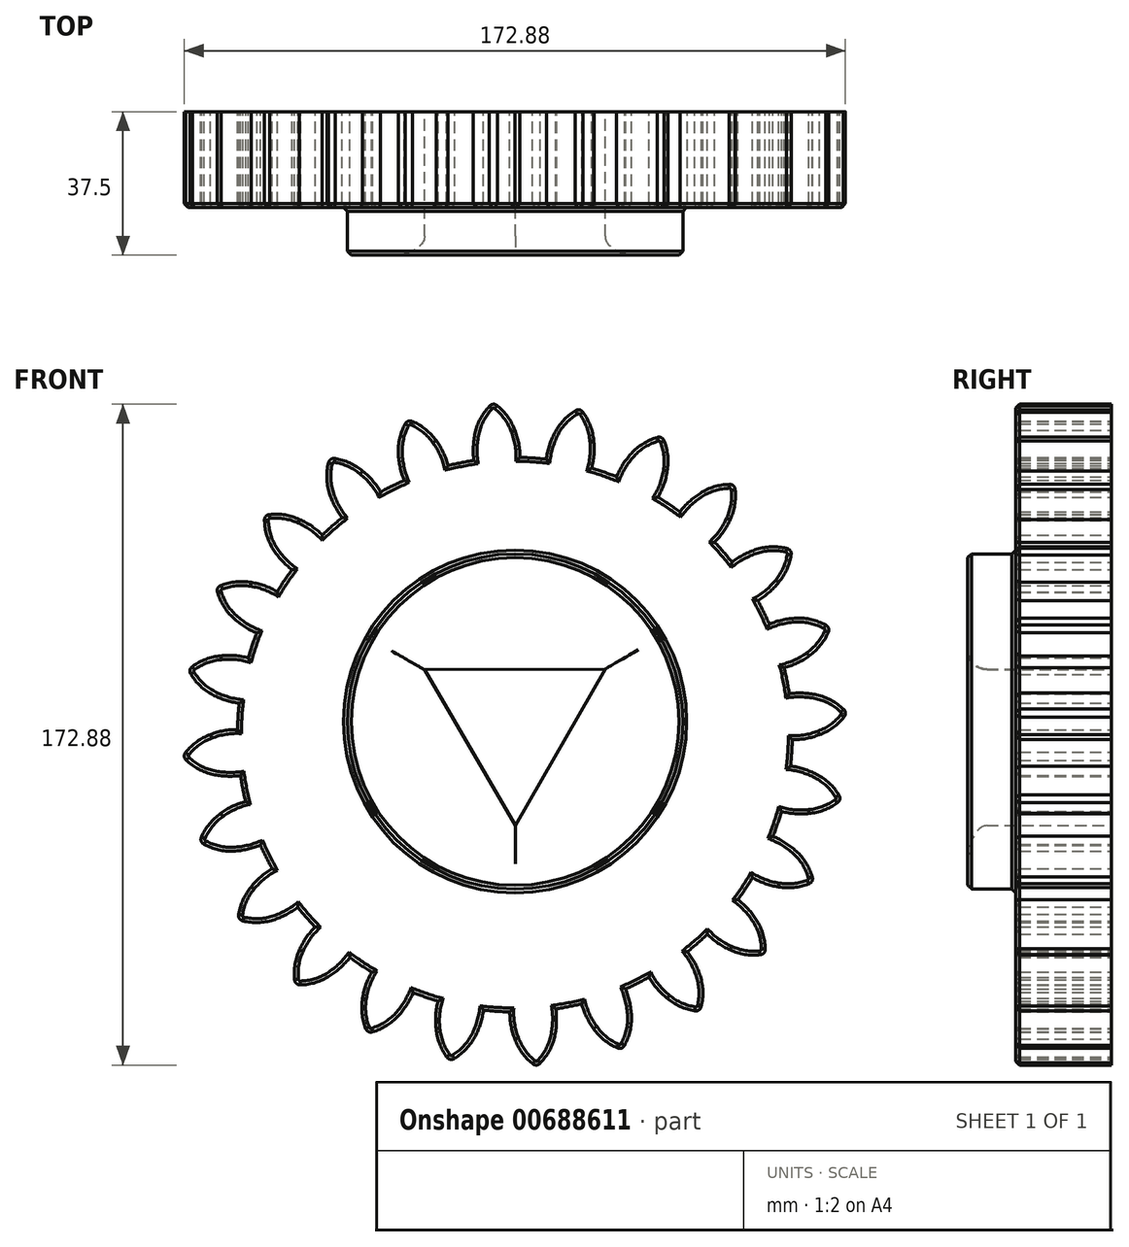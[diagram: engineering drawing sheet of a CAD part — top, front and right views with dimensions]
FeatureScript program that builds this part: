
annotation { "Feature Type Name" : "Feature", "Feature Type Description" : "" }
export const myFeature = defineFeature(function(context is Context, id is Id, definition is map)
    precondition{}
    {
        {
            var Q0;
            Q0=qCreatedBy(makeId("Front.planeOp"),FACE);
            var sketch = newSketch(context, id + "F0", { "sketchPlane" : qUnion([Q0])});
            skCircle(sketch, "E0", {"center": v(-0.05, -3.44) * mm, "radius": 86.16 * mm, "construction": true});
            skCircle(sketch, "E1", {"center": v(-0.05, -3.44) * mm, "radius": 79.67 * mm, "construction": true});
            skCircle(sketch, "E2", {"center": v(-0.05, -3.44) * mm, "radius": 72.52 * mm});
            skLineSegment(sketch, "E3", {"start": v(-0.05, -3.44) * mm, "end": v(-0.05, 109) * mm, "construction": true});
            skLineSegment(sketch, "E4", {"start": v(-0.05, -3.44) * mm, "end": v(-7.36, 108.12) * mm, "construction": true});
            skCircle(sketch, "E5", {"center": v(-0.05, -3.44) * mm, "radius": 74.83 * mm, "construction": true});
            skLineSegment(sketch, "E6", {"start": v(-0.05, 76.19) * mm, "end": v(-82.1, 46.32) * mm, "construction": true});
            skLineSegment(sketch, "E7", {"start": v(-0.05, 76.19) * mm, "end": v(-80.24, 76.19) * mm, "construction": true});
            skCircle(sketch, "E8", {"center": v(-0.05, 76.19) * mm, "radius": 14.6 * mm, "construction": true});
            skCircle(sketch, "E9", {"center": v(-13.78, 71.2) * mm, "radius": 14.6 * mm, "construction": true});
            skArc(sketch, "E10", {"start": v(-0.05, 76.19) * mm, "mid": v(-1.9, 79.7) * mm, "end": v(-4.65, 82.6) * mm});
            skArc(sketch, "E11.MirrorCS", {"start": v(-10.45, 75.5) * mm, "mid": v(-9.06, 79.24) * mm, "end": v(-6.73, 82.46) * mm});
            skArc(sketch, "E12", {"start": v(-4.65, 82.6) * mm, "mid": v(-5.72, 83) * mm, "end": v(-6.73, 82.46) * mm});
            skArc(sketch, "E13", {"start": v(-10.45, 75.5) * mm, "mid": v(-10.91, 71.91) * mm, "end": v(-10.77, 68.29) * mm});
            skArc(sketch, "E14", {"start": v(1.27, 69.07) * mm, "mid": v(0.96, 72.7) * mm, "end": v(-0.05, 76.19) * mm});
            skPoint(sketch, "E15.0.midPoint", {"position": v(-0.05, 17.48) * mm});
            skCircle(sketch, "E16", {"center": v(0, 0) * mm, "radius": 48.64 * mm});
            skCircle(sketch, "E17.cCircle", {"center": v(0, 0) * mm, "radius": 13.62 * mm, "construction": true});
            skLineSegment(sketch, "E17.0", {"start": v(-23.64, 13.53) * mm, "end": v(23.53, 13.7) * mm});
            skLineSegment(sketch, "E17.1", {"start": v(23.53, 13.7) * mm, "end": v(0.1, -27.23) * mm});
            skLineSegment(sketch, "E17.2", {"start": v(0.1, -27.23) * mm, "end": v(-23.64, 13.53) * mm});
            skPoint(sketch, "E17.0.midPoint", {"position": v(-0.05, 13.62) * mm});
            skSolve(sketch);
        }
        {
            var Q0;
            {var subQ0=sQuery(id+"F0.wireOp",EDGE,"E2");var subQ1=makeQuery(id+"F0.imprint","INTERSECT",VERTEX,{"derivedFrom":[subQ0,sQuery(id+"F0.wireOp",EDGE,"E13")]});Q0=makeQuery(id+"F0.imprint","IMPRINT",FACE,{"disambiguationData":[TD([[makeQuery(id+"F0.imprint","IMPRINT",EDGE,{"disambiguationData":[TD([[subQ1,1.0]])],"derivedFrom":subQ0}),1.0]])]});}
            var Q1;
            Q1=makeQuery(id+"F0.imprint","IMPRINT",FACE,{"disambiguationData":[TD([[makeQuery(id+"F0.imprint","IMPRINT",EDGE,{"derivedFrom":sQuery(id+"F0.wireOp",EDGE,"E10")}),1.0]])]});
            var Q2;
            Q2=makeQuery(id+"F0.imprint","IMPRINT",FACE,{"disambiguationData":[TD([[makeQuery(id+"F0.imprint","IMPRINT",EDGE,{"derivedFrom":sQuery(id+"F0.wireOp",EDGE,"E16")}),1.0]])]});
            extrude(context, id + "F1", {"entities" : qUnion([Q0, Q1, Q2]), "endBound" : BoundingType.SYMMETRIC, "depth" : 25 * mm, "offsetDistance" : 25 * mm});
        }
        {
            var Q0;
            Q0=makeQuery(id+"F1.opExtrude","SWEPT_BODY",BODY,{"disambiguationData":[OSD([sQuery(id+"F0.wireOp",EDGE,"E2"),sQuery(id+"F0.wireOp",EDGE,"E10"),sQuery(id+"F0.wireOp",EDGE,"E11.MirrorCS"),sQuery(id+"F0.wireOp",EDGE,"E12"),sQuery(id+"F0.wireOp",EDGE,"E13"),sQuery(id+"F0.wireOp",EDGE,"E14")])]});
            var Q1;
            Q1=makeQuery(id+"F1.opExtrude","SWEPT_FACE",FACE,{"disambiguationData":[OSD([sQuery(id+"F0.wireOp",EDGE,"E2")])]});
            circularPattern(context, id + "F2", {"entities" : qUnion([Q0]), "axis" : qUnion([Q1]), "angle" : 360 * degree, "instanceCount" : 24, "equalSpace" : true});
        }
        {
            var Q0;
            Q0=makeQuery(id+"F1.opExtrude","CAP_FACE",FACE,{"disambiguationData":[OSD([sQuery(id+"F0.wireOp",EDGE,"E2"),sQuery(id+"F0.wireOp",EDGE,"E10"),sQuery(id+"F0.wireOp",EDGE,"E11.MirrorCS"),sQuery(id+"F0.wireOp",EDGE,"E12"),sQuery(id+"F0.wireOp",EDGE,"E13"),sQuery(id+"F0.wireOp",EDGE,"E14"),sQuery(id+"F0.wireOp",EDGE,"E17.0"),sQuery(id+"F0.wireOp",EDGE,"E17.1"),sQuery(id+"F0.wireOp",EDGE,"E17.2")])],"isStart":false});
            var sketch = newSketch(context, id + "F3", { "sketchPlane" : qUnion([Q0])});
            skCircle(sketch, "E18", {"center": v(0, 0) * mm, "radius": 43.85 * mm});
            skSolve(sketch);
        }
        {
            var Q0;
            Q0=makeQuery(id+"F3.imprint","IMPRINT",FACE,{"disambiguationData":[TD([[makeQuery(id+"F3.imprint","IMPRINT",EDGE,{"derivedFrom":sQuery(id+"F3.wireOp",EDGE,"E18")}),1.0]])]});
            extrude(context, id + "F4", {"entities" : qUnion([Q0]), "operationType" : NewBodyOperationType.ADD, "endBound" : BoundingType.SYMMETRIC, "depth" : 25 * mm, "offsetDistance" : 25 * mm});
        }
        {
            var Q0;
            Q0=makeQuery(id+"F4.opExtrude","CAP_EDGE",EDGE,{"disambiguationData":[OSD([sQuery(id+"F0.wireOp",EDGE,"E17.0")])],"isStart":false});
            var Q1;
            Q1=makeQuery(id+"F4.opExtrude","CAP_EDGE",EDGE,{"disambiguationData":[OSD([sQuery(id+"F0.wireOp",EDGE,"E17.2")])],"isStart":false});
            var Q2;
            Q2=makeQuery(id+"F4.opExtrude","CAP_EDGE",EDGE,{"disambiguationData":[OSD([sQuery(id+"F0.wireOp",EDGE,"E17.1")])],"isStart":false});
            fillet(context, id + "F5", {"entities" : qUnion([Q0, Q1, Q2]), "radius" : 5 * mm, "tangentPropagation" : true, "allowEdgeOverflow" : false});
        }
        {
            var Q0;
            {var subQ0=makeQuery(id+"F1.opExtrude","CAP_FACE",FACE,{"disambiguationData":[OSD([sQuery(id+"F0.wireOp",EDGE,"E2"),sQuery(id+"F0.wireOp",EDGE,"E10"),sQuery(id+"F0.wireOp",EDGE,"E11.MirrorCS"),sQuery(id+"F0.wireOp",EDGE,"E12"),sQuery(id+"F0.wireOp",EDGE,"E13"),sQuery(id+"F0.wireOp",EDGE,"E14"),sQuery(id+"F0.wireOp",EDGE,"E17.0"),sQuery(id+"F0.wireOp",EDGE,"E17.1"),sQuery(id+"F0.wireOp",EDGE,"E17.2")])],"isStart":false});Q0=makeQuery(id+"F4.boolean.opBoolean","MERGE",FACE,{"derivedFrom":[makeQuery(id+"F2.opPattern","COPY",FACE,{"derivedFrom":subQ0,"instanceName":"1"}),makeQuery(id+"F2.opPattern","COPY",FACE,{"derivedFrom":subQ0,"instanceName":"2"}),makeQuery(id+"F2.opPattern","COPY",FACE,{"derivedFrom":subQ0,"instanceName":"3"}),makeQuery(id+"F2.opPattern","COPY",FACE,{"derivedFrom":subQ0,"instanceName":"4"}),makeQuery(id+"F2.opPattern","COPY",FACE,{"derivedFrom":subQ0,"instanceName":"5"}),makeQuery(id+"F2.opPattern","COPY",FACE,{"derivedFrom":subQ0,"instanceName":"6"}),makeQuery(id+"F2.opPattern","COPY",FACE,{"derivedFrom":subQ0,"instanceName":"7"}),makeQuery(id+"F2.opPattern","COPY",FACE,{"derivedFrom":subQ0,"instanceName":"8"}),makeQuery(id+"F2.opPattern","COPY",FACE,{"derivedFrom":subQ0,"instanceName":"9"}),makeQuery(id+"F2.opPattern","COPY",FACE,{"derivedFrom":subQ0,"instanceName":"10"}),makeQuery(id+"F2.opPattern","COPY",FACE,{"derivedFrom":subQ0,"instanceName":"11"}),makeQuery(id+"F2.opPattern","COPY",FACE,{"derivedFrom":subQ0,"instanceName":"12"}),makeQuery(id+"F2.opPattern","COPY",FACE,{"derivedFrom":subQ0,"instanceName":"13"}),makeQuery(id+"F2.opPattern","COPY",FACE,{"derivedFrom":subQ0,"instanceName":"14"}),makeQuery(id+"F2.opPattern","COPY",FACE,{"derivedFrom":subQ0,"instanceName":"15"}),makeQuery(id+"F2.opPattern","COPY",FACE,{"derivedFrom":subQ0,"instanceName":"16"}),makeQuery(id+"F2.opPattern","COPY",FACE,{"derivedFrom":subQ0,"instanceName":"17"}),makeQuery(id+"F2.opPattern","COPY",FACE,{"derivedFrom":subQ0,"instanceName":"18"}),makeQuery(id+"F2.opPattern","COPY",FACE,{"derivedFrom":subQ0,"instanceName":"19"}),makeQuery(id+"F2.opPattern","COPY",FACE,{"derivedFrom":subQ0,"instanceName":"20"}),makeQuery(id+"F2.opPattern","COPY",FACE,{"derivedFrom":subQ0,"instanceName":"21"}),makeQuery(id+"F2.opPattern","COPY",FACE,{"derivedFrom":subQ0,"instanceName":"22"}),makeQuery(id+"F2.opPattern","COPY",FACE,{"derivedFrom":subQ0,"instanceName":"23"})]});}
            extrude(context, id + "F6", {"entities" : qUnion([Q0]), "operationType" : NewBodyOperationType.REMOVE, "oppositeDirection" : true, "depth" : 30 * mm, "offsetDistance" : 25 * mm});
        }
        {
            var Q0;
            Q0=makeQuery(id+"F4.opExtrude","CAP_EDGE",EDGE,{"disambiguationData":[OSD([sQuery(id+"F3.wireOp",EDGE,"E18")])],"isStart":false});
            var Q1;
            {var subQ0=makeQuery(id+"F1.opExtrude","CAP_FACE",FACE,{"disambiguationData":[OSD([sQuery(id+"F0.wireOp",EDGE,"E2"),sQuery(id+"F0.wireOp",EDGE,"E10"),sQuery(id+"F0.wireOp",EDGE,"E11.MirrorCS"),sQuery(id+"F0.wireOp",EDGE,"E12"),sQuery(id+"F0.wireOp",EDGE,"E13"),sQuery(id+"F0.wireOp",EDGE,"E14"),sQuery(id+"F0.wireOp",EDGE,"E17.0"),sQuery(id+"F0.wireOp",EDGE,"E17.1"),sQuery(id+"F0.wireOp",EDGE,"E17.2")])],"isStart":false});Q1=makeQuery(id+"F4.boolean.opBoolean","MERGE",FACE,{"derivedFrom":[subQ0,makeQuery(id+"F2.opPattern","COPY",FACE,{"derivedFrom":subQ0,"instanceName":"1"}),makeQuery(id+"F2.opPattern","COPY",FACE,{"derivedFrom":subQ0,"instanceName":"2"}),makeQuery(id+"F2.opPattern","COPY",FACE,{"derivedFrom":subQ0,"instanceName":"3"}),makeQuery(id+"F2.opPattern","COPY",FACE,{"derivedFrom":subQ0,"instanceName":"4"}),makeQuery(id+"F2.opPattern","COPY",FACE,{"derivedFrom":subQ0,"instanceName":"5"}),makeQuery(id+"F2.opPattern","COPY",FACE,{"derivedFrom":subQ0,"instanceName":"6"}),makeQuery(id+"F2.opPattern","COPY",FACE,{"derivedFrom":subQ0,"instanceName":"7"}),makeQuery(id+"F2.opPattern","COPY",FACE,{"derivedFrom":subQ0,"instanceName":"8"}),makeQuery(id+"F2.opPattern","COPY",FACE,{"derivedFrom":subQ0,"instanceName":"9"}),makeQuery(id+"F2.opPattern","COPY",FACE,{"derivedFrom":subQ0,"instanceName":"10"}),makeQuery(id+"F2.opPattern","COPY",FACE,{"derivedFrom":subQ0,"instanceName":"11"}),makeQuery(id+"F2.opPattern","COPY",FACE,{"derivedFrom":subQ0,"instanceName":"12"}),makeQuery(id+"F2.opPattern","COPY",FACE,{"derivedFrom":subQ0,"instanceName":"13"}),makeQuery(id+"F2.opPattern","COPY",FACE,{"derivedFrom":subQ0,"instanceName":"14"}),makeQuery(id+"F2.opPattern","COPY",FACE,{"derivedFrom":subQ0,"instanceName":"15"}),makeQuery(id+"F2.opPattern","COPY",FACE,{"derivedFrom":subQ0,"instanceName":"16"}),makeQuery(id+"F2.opPattern","COPY",FACE,{"derivedFrom":subQ0,"instanceName":"17"}),makeQuery(id+"F2.opPattern","COPY",FACE,{"derivedFrom":subQ0,"instanceName":"18"}),makeQuery(id+"F2.opPattern","COPY",FACE,{"derivedFrom":subQ0,"instanceName":"19"}),makeQuery(id+"F2.opPattern","COPY",FACE,{"derivedFrom":subQ0,"instanceName":"20"}),makeQuery(id+"F2.opPattern","COPY",FACE,{"derivedFrom":subQ0,"instanceName":"21"}),makeQuery(id+"F2.opPattern","COPY",FACE,{"derivedFrom":subQ0,"instanceName":"22"}),makeQuery(id+"F2.opPattern","COPY",FACE,{"derivedFrom":subQ0,"instanceName":"23"})]});}
            chamfer(context, id + "F7", {"entities" : qUnion([Q0, Q1]), "width" : 1 * mm, "tangentPropagation" : true});
        }
    });
